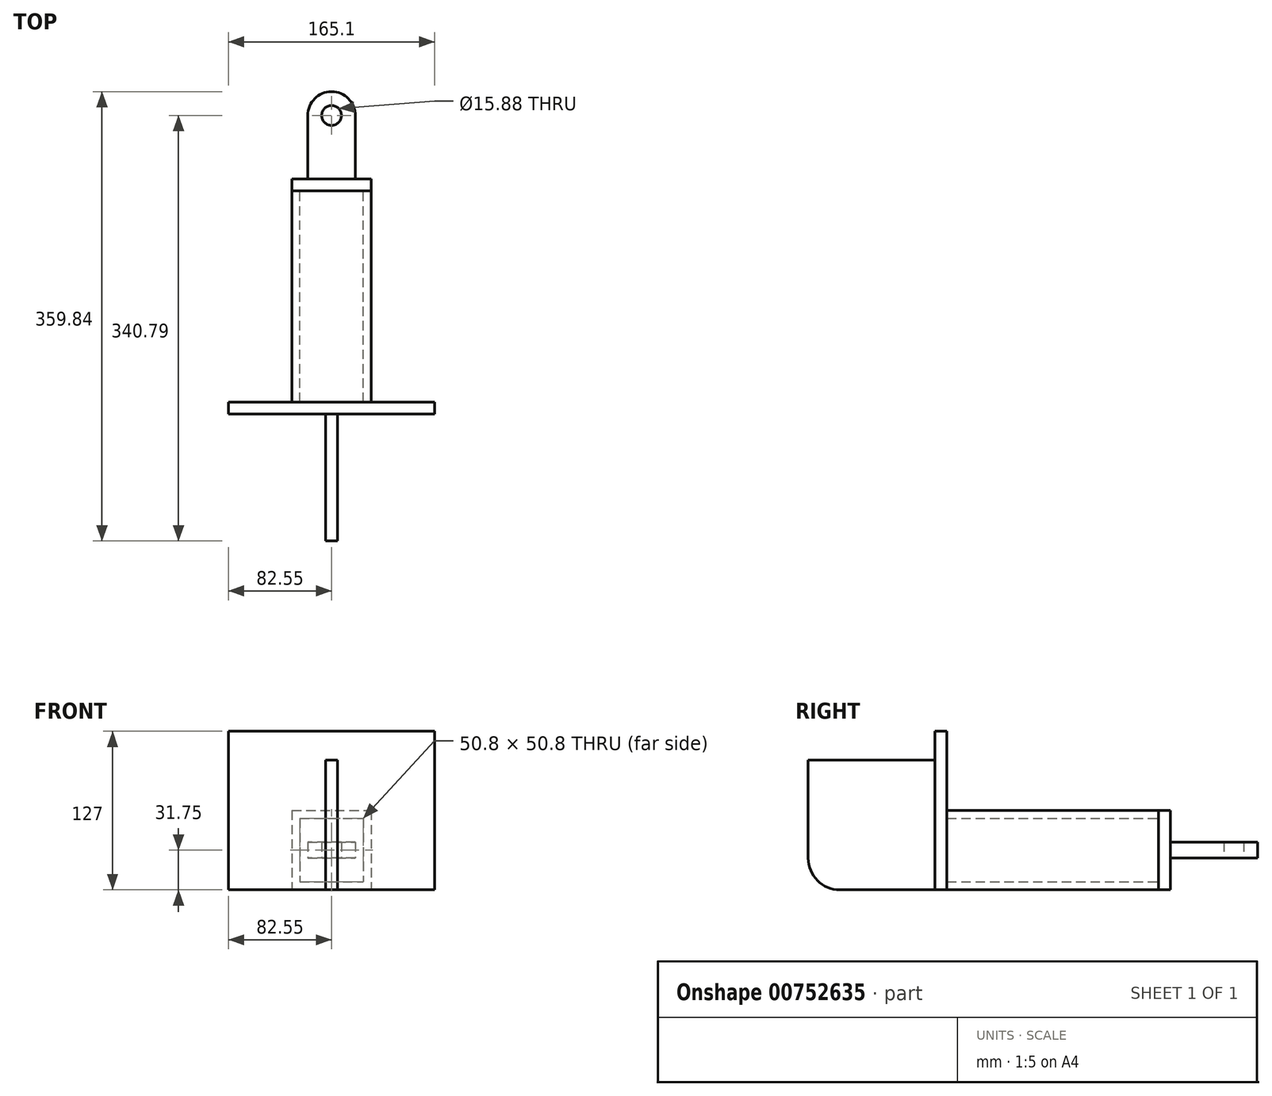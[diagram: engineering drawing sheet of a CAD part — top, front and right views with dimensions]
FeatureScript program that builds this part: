
annotation { "Feature Type Name" : "Feature", "Feature Type Description" : "" }
export const myFeature = defineFeature(function(context is Context, id is Id, definition is map)
    precondition{}
    {
        {
            var Q0;
            Q0=qCreatedBy(makeId("Top.planeOp"),FACE);
            var sketch = newSketch(context, id + "F0", { "sketchPlane" : qUnion([Q0])});
            skArc(sketch, "E0", {"start": v(19.05, 0) * mm, "mid": v(0, 19.05) * mm, "end": v(-19.05, 0) * mm});
            skLineSegment(sketch, "E1.0", {"start": v(-19.05, 0) * mm, "end": v(-19.05, -50.8) * mm});
            skLineSegment(sketch, "E2.0", {"start": v(19.05, 0) * mm, "end": v(19.05, -50.8) * mm});
            skLineSegment(sketch, "E3.0", {"start": v(-19.05, -50.8) * mm, "end": v(19.05, -50.8) * mm});
            skCircle(sketch, "E4", {"center": v(0, 0) * mm, "radius": 7.94 * mm});
            skSolve(sketch);
        }
        {
            var Q0;
            Q0=makeQuery(id+"F0.imprint","IMPRINT",FACE,{"disambiguationData":[TD([[makeQuery(id+"F0.imprint","IMPRINT",EDGE,{"derivedFrom":sQuery(id+"F0.wireOp",EDGE,"E0")}),1.0]])]});
            extrude(context, id + "F1", {"entities" : qUnion([Q0]), "depth" : 6.35 * mm, "offsetDistance" : 25.4 * mm, "hasSecondDirection" : true, "secondDirectionOppositeDirection" : true, "secondDirectionDepth" : 6.35 * mm});
        }
        {
            var Q0;
            Q0=makeQuery(id+"F1.opExtrude","SWEPT_FACE",FACE,{"disambiguationData":[OSD([sQuery(id+"F0.wireOp",EDGE,"E3.0")])]});
            var sketch = newSketch(context, id + "F2", { "sketchPlane" : qUnion([Q0])});
            skLineSegment(sketch, "E5.bottom", {"start": v(-31.75, 31.75) * mm, "end": v(31.75, 31.75) * mm});
            skLineSegment(sketch, "E5.top", {"start": v(-31.75, -31.75) * mm, "end": v(31.75, -31.75) * mm});
            skLineSegment(sketch, "E5.left", {"start": v(-31.75, 31.75) * mm, "end": v(-31.75, -31.75) * mm});
            skLineSegment(sketch, "E5.right", {"start": v(31.75, 31.75) * mm, "end": v(31.75, -31.75) * mm});
            skSolve(sketch);
        }
        {
            var Q0;
            Q0 = qSketchRegion(id + "F2", true);
            extrude(context, id + "F3", {"entities" : qUnion([Q0]), "operationType" : NewBodyOperationType.ADD, "depth" : 9.52 * mm, "offsetDistance" : 25.4 * mm});
        }
        {
            var Q0;
            Q0=makeQuery(id+"F3.opExtrude","CAP_FACE",FACE,{"disambiguationData":[OSD([sQuery(id+"F2.wireOp",EDGE,"E5.bottom"),sQuery(id+"F2.wireOp",EDGE,"E5.top"),sQuery(id+"F2.wireOp",EDGE,"E5.left"),sQuery(id+"F2.wireOp",EDGE,"E5.right")])],"isStart":false});
            var sketch = newSketch(context, id + "F4", { "sketchPlane" : qUnion([Q0])});
            skLineSegment(sketch, "E6.bottom", {"start": v(-31.75, 31.75) * mm, "end": v(31.75, 31.75) * mm});
            skLineSegment(sketch, "E6.top", {"start": v(-31.75, -31.75) * mm, "end": v(31.75, -31.75) * mm});
            skLineSegment(sketch, "E6.left", {"start": v(-31.75, 31.75) * mm, "end": v(-31.75, -31.75) * mm});
            skLineSegment(sketch, "E6.right", {"start": v(31.75, 31.75) * mm, "end": v(31.75, -31.75) * mm});
            skLineSegment(sketch, "E7.0", {"start": v(-25.4, 25.4) * mm, "end": v(25.4, 25.4) * mm});
            skLineSegment(sketch, "E7.1", {"start": v(-25.4, 25.4) * mm, "end": v(-25.4, -25.4) * mm});
            skLineSegment(sketch, "E7.2", {"start": v(-25.4, -25.4) * mm, "end": v(25.4, -25.4) * mm});
            skLineSegment(sketch, "E7.3", {"start": v(25.4, 25.4) * mm, "end": v(25.4, -25.4) * mm});
            skSolve(sketch);
        }
        {
            var Q0;
            Q0 = qSketchRegion(id + "F4", true);
            extrude(context, id + "F5", {"entities" : qUnion([Q0]), "depth" : 169.34 * mm, "offsetDistance" : 25.4 * mm});
        }
        {
            var Q0;
            Q0=makeQuery(id+"F5.opExtrude","CAP_FACE",FACE,{"disambiguationData":[OSD([sQuery(id+"F4.wireOp",EDGE,"E6.bottom"),sQuery(id+"F4.wireOp",EDGE,"E6.top"),sQuery(id+"F4.wireOp",EDGE,"E6.left"),sQuery(id+"F4.wireOp",EDGE,"E6.right"),sQuery(id+"F4.wireOp",EDGE,"E7.0"),sQuery(id+"F4.wireOp",EDGE,"E7.1"),sQuery(id+"F4.wireOp",EDGE,"E7.2"),sQuery(id+"F4.wireOp",EDGE,"E7.3")])],"isStart":false});
            var sketch = newSketch(context, id + "F6", { "sketchPlane" : qUnion([Q0])});
            skLineSegment(sketch, "E8.bottom", {"start": v(-82.55, -31.75) * mm, "end": v(82.55, -31.75) * mm});
            skLineSegment(sketch, "E8.top", {"start": v(-82.55, 95.25) * mm, "end": v(82.55, 95.25) * mm});
            skLineSegment(sketch, "E8.left", {"start": v(-82.55, -31.75) * mm, "end": v(-82.55, 95.25) * mm});
            skLineSegment(sketch, "E8.right", {"start": v(82.55, -31.75) * mm, "end": v(82.55, 95.25) * mm});
            skSolve(sketch);
        }
        {
            var Q0;
            Q0 = qSketchRegion(id + "F6", true);
            extrude(context, id + "F7", {"entities" : qUnion([Q0]), "depth" : 9.52 * mm, "offsetDistance" : 25.4 * mm});
        }
        {
            var Q0;
            Q0=qCreatedBy(makeId("Right.planeOp"),FACE);
            var sketch = newSketch(context, id + "F8", { "sketchPlane" : qUnion([Q0])});
            skLineSegment(sketch, "E9.bottom", {"start": v(-239.19, -31.75) * mm, "end": v(-315.39, -31.75) * mm});
            skLineSegment(sketch, "E9.top", {"start": v(-239.19, 72.26) * mm, "end": v(-340.79, 72.26) * mm});
            skLineSegment(sketch, "E9.left", {"start": v(-239.19, -31.75) * mm, "end": v(-239.19, 72.26) * mm});
            skLineSegment(sketch, "E9.right", {"start": v(-340.79, -6.35) * mm, "end": v(-340.79, 72.26) * mm});
            skPoint(sketch, "E10.visualSharp", {"position": v(-340.79, -31.75) * mm});
            skArc(sketch, "E10.filletArc", {"start": v(-340.79, -6.35) * mm, "mid": v(-333.35, -24.31) * mm, "end": v(-315.39, -31.75) * mm});
            skSolve(sketch);
        }
        {
            var Q0;
            Q0=makeQuery(id+"F8.imprint","IMPRINT",FACE,{"disambiguationData":[TD([[makeQuery(id+"F8.imprint","IMPRINT",EDGE,{"derivedFrom":sQuery(id+"F8.wireOp",EDGE,"E9.bottom")}),-1.0]])]});
            var Q1;
            Q1 = qConstructionFilter(qBodyType(qCreatedBy(id + "F8" ,EDGE), BodyType.WIRE), ConstructionObject.NO);
            extrude(context, id + "F9", {"entities" : qUnion([Q0]), "surfaceEntities" : qUnion([Q1]), "depth" : 4.76 * mm, "offsetDistance" : 25.4 * mm, "hasSecondDirection" : true, "secondDirectionOppositeDirection" : true, "secondDirectionDepth" : 4.76 * mm});
        }
    });
